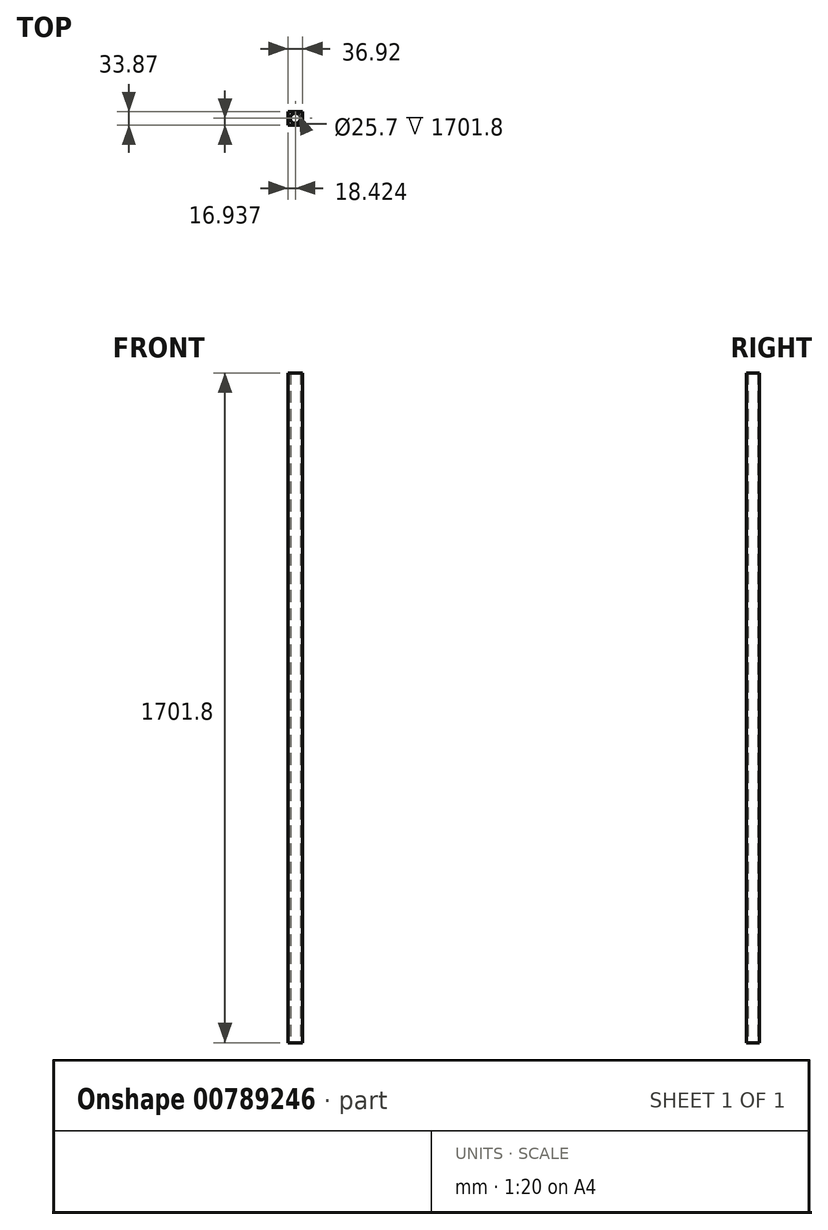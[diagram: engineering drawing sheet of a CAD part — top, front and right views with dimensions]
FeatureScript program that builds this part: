
annotation { "Feature Type Name" : "Feature", "Feature Type Description" : "" }
export const myFeature = defineFeature(function(context is Context, id is Id, definition is map)
    precondition{}
    {
        {
            var Q0;
            Q0=qCreatedBy(makeId("Top.planeOp"),FACE);
            var sketch = newSketch(context, id + "F0", { "sketchPlane" : qUnion([Q0])});
            skLineSegment(sketch, "E0.bottom", {"start": v(-3.01, 19.62) * mm, "end": v(-39.93, 19.62) * mm});
            skLineSegment(sketch, "E0.top", {"start": v(-3.01, 53.49) * mm, "end": v(-39.93, 53.49) * mm});
            skLineSegment(sketch, "E0.left", {"start": v(-3.01, 19.62) * mm, "end": v(-3.01, 53.49) * mm});
            skLineSegment(sketch, "E0.right", {"start": v(-39.93, 19.62) * mm, "end": v(-39.93, 53.49) * mm});
            skPoint(sketch, "E0.middle", {"position": v(-21.47, 36.56) * mm});
            skSolve(sketch);
        }
        {
            var Q0;
            Q0=makeQuery(id+"F0.imprint","IMPRINT",FACE,{"disambiguationData":[TD([[makeQuery(id+"F0.imprint","IMPRINT",EDGE,{"derivedFrom":sQuery(id+"F0.wireOp",EDGE,"E0.bottom")}),-1.0]])]});
            extrude(context, id + "F1", {"entities" : qUnion([Q0]), "depth" : 1701.8 * mm, "offsetDistance" : 25.4 * mm});
        }
        {
            var Q0;
            Q0=makeQuery(id+"F1.opExtrude","CAP_FACE",FACE,{"disambiguationData":[OSD([sQuery(id+"F0.wireOp",EDGE,"E0.bottom"),sQuery(id+"F0.wireOp",EDGE,"E0.top"),sQuery(id+"F0.wireOp",EDGE,"E0.left"),sQuery(id+"F0.wireOp",EDGE,"E0.right")])],"isStart":true});
            var sketch = newSketch(context, id + "F2", { "sketchPlane" : qUnion([Q0])});
            skCircle(sketch, "E1", {"center": v(-21.5, -36.56) * mm, "radius": 12.85 * mm});
            skPoint(sketch, "E1.centerSnap0", {"position": v(-39.93, -36.56) * mm});
            skSolve(sketch);
        }
        {
            var Q0;
            Q0=makeQuery(id+"F2.imprint","IMPRINT",FACE,{"disambiguationData":[TD([[makeQuery(id+"F2.imprint","IMPRINT",EDGE,{"derivedFrom":sQuery(id+"F2.wireOp",EDGE,"E1")}),1.0]])]});
            extrude(context, id + "F3", {"entities" : qUnion([Q0]), "operationType" : NewBodyOperationType.REMOVE, "oppositeDirection" : true, "depth" : 1701.8 * mm, "offsetDistance" : 25.4 * mm});
        }
    });
